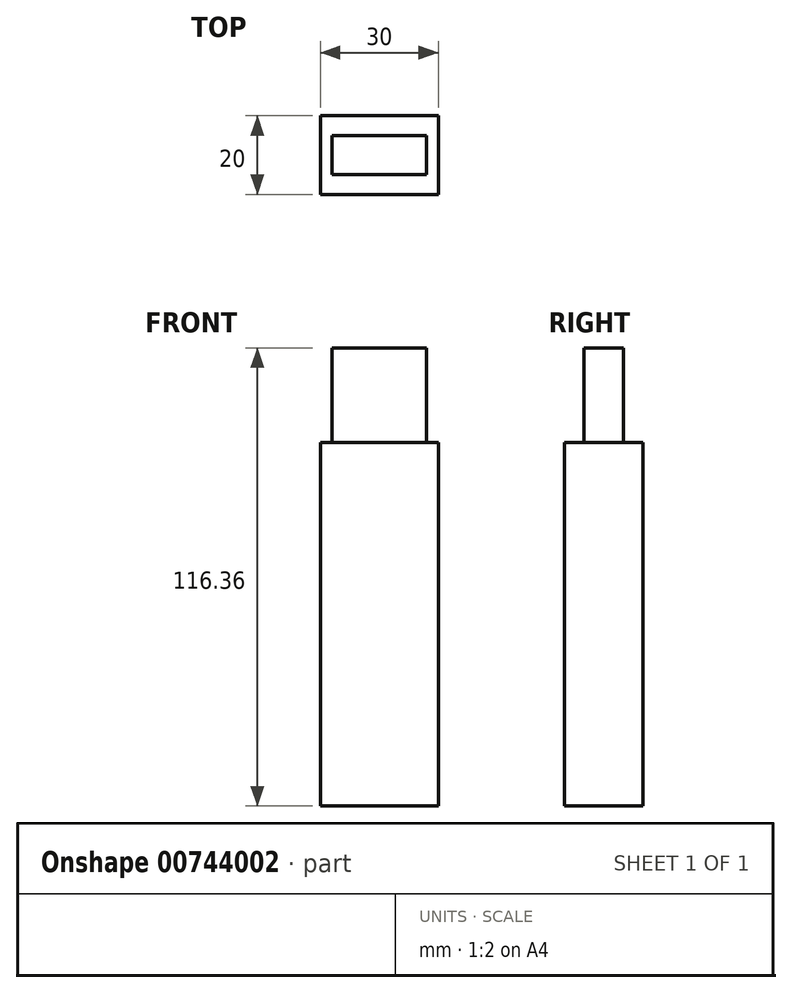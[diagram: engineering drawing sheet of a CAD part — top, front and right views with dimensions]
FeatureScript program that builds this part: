
annotation { "Feature Type Name" : "Feature", "Feature Type Description" : "" }
export const myFeature = defineFeature(function(context is Context, id is Id, definition is map)
    precondition{}
    {
        {
            var Q0;
            Q0=qCreatedBy(makeId("Front.planeOp"),FACE);
            var sketch = newSketch(context, id + "F0", { "sketchPlane" : qUnion([Q0])});
            skLineSegment(sketch, "E0.bottom", {"start": v(12, 46.18) * mm, "end": v(-12, 46.18) * mm});
            skLineSegment(sketch, "E0.top", {"start": v(12, 70.18) * mm, "end": v(-12, 70.18) * mm});
            skLineSegment(sketch, "E0.left", {"start": v(12, 46.18) * mm, "end": v(12, 70.18) * mm});
            skLineSegment(sketch, "E0.right", {"start": v(-12, 46.18) * mm, "end": v(-12, 70.18) * mm});
            skPoint(sketch, "E0.middle", {"position": v(0, 58.18) * mm});
            skLineSegment(sketch, "E1.bottom", {"start": v(-15, 46.18) * mm, "end": v(15, 46.18) * mm});
            skLineSegment(sketch, "E1.top", {"start": v(-15, -46.18) * mm, "end": v(15, -46.18) * mm});
            skLineSegment(sketch, "E1.left", {"start": v(-15, 46.18) * mm, "end": v(-15, -46.18) * mm});
            skLineSegment(sketch, "E1.right", {"start": v(15, 46.18) * mm, "end": v(15, -46.18) * mm});
            skPoint(sketch, "E1.middle", {"position": v(0, 0) * mm});
            skLineSegment(sketch, "E2.bottom", {"start": v(-15, -46.18) * mm, "end": v(0, -46.18) * mm});
            skLineSegment(sketch, "E2.top", {"start": v(-15, -78.18) * mm, "end": v(0, -78.18) * mm});
            skLineSegment(sketch, "E2.left", {"start": v(-15, -46.18) * mm, "end": v(-15, -78.18) * mm});
            skLineSegment(sketch, "E2.right", {"start": v(0, -46.18) * mm, "end": v(0, -78.18) * mm});
            skLineSegment(sketch, "E3.bottom", {"start": v(15, -46.18) * mm, "end": v(0, -46.18) * mm});
            skLineSegment(sketch, "E3.top", {"start": v(15, -78.18) * mm, "end": v(0, -78.18) * mm});
            skLineSegment(sketch, "E3.left", {"start": v(15, -46.18) * mm, "end": v(15, -78.18) * mm});
            skLineSegment(sketch, "E4.bottom", {"start": v(-15, 46.18) * mm, "end": v(-26, 46.18) * mm});
            skLineSegment(sketch, "E4.top", {"start": v(-15, -20.82) * mm, "end": v(-26, -20.82) * mm});
            skLineSegment(sketch, "E4.left", {"start": v(-15, 46.18) * mm, "end": v(-15, -20.82) * mm});
            skLineSegment(sketch, "E4.right", {"start": v(-26, 46.18) * mm, "end": v(-26, -20.82) * mm});
            skLineSegment(sketch, "E5.bottom", {"start": v(15, 46.18) * mm, "end": v(26, 46.18) * mm});
            skLineSegment(sketch, "E5.top", {"start": v(15, -20.82) * mm, "end": v(26, -20.82) * mm});
            skLineSegment(sketch, "E5.left", {"start": v(15, 46.18) * mm, "end": v(15, -20.82) * mm});
            skLineSegment(sketch, "E5.right", {"start": v(26, 46.18) * mm, "end": v(26, -20.82) * mm});
            skLineSegment(sketch, "E6.top", {"start": v(-15, -142.18) * mm, "end": v(0, -142.18) * mm});
            skLineSegment(sketch, "E6.left", {"start": v(-15, -78.18) * mm, "end": v(-15, -142.18) * mm});
            skLineSegment(sketch, "E6.right", {"start": v(0, -78.18) * mm, "end": v(0, -142.18) * mm});
            skLineSegment(sketch, "E7.top", {"start": v(15, -142.18) * mm, "end": v(0, -142.18) * mm});
            skLineSegment(sketch, "E7.left", {"start": v(15, -78.18) * mm, "end": v(15, -142.18) * mm});
            skLineSegment(sketch, "E8.bottom", {"start": v(0, -78.18) * mm, "end": v(-15, -78.18) * mm});
            skLineSegment(sketch, "E8.top", {"start": v(0, -110.18) * mm, "end": v(-15, -110.18) * mm});
            skLineSegment(sketch, "E8.left", {"start": v(0, -78.18) * mm, "end": v(0, -110.18) * mm});
            skLineSegment(sketch, "E8.right", {"start": v(-15, -78.18) * mm, "end": v(-15, -110.18) * mm});
            skLineSegment(sketch, "E9.top", {"start": v(15, -110.18) * mm, "end": v(0, -110.18) * mm});
            skLineSegment(sketch, "E9.left", {"start": v(15, -78.18) * mm, "end": v(15, -110.18) * mm});
            skSolve(sketch);
        }
        {
            var Q0;
            Q0=makeQuery(id+"F0.imprint","IMPRINT",FACE,{"disambiguationData":[TD([[makeQuery(id+"F0.imprint","IMPRINT",EDGE,{"derivedFrom":sQuery(id+"F0.wireOp",EDGE,"E1.left")}),1.0]])]});
            extrude(context, id + "F1", {"entities" : qUnion([Q0]), "depth" : 10 * mm, "offsetDistance" : 25 * mm});
        }
        {
            var Q0;
            Q0=makeQuery(id+"F0.imprint","IMPRINT",FACE,{"disambiguationData":[TD([[makeQuery(id+"F0.imprint","IMPRINT",EDGE,{"derivedFrom":sQuery(id+"F0.wireOp",EDGE,"E1.left")}),1.0]])]});
            extrude(context, id + "F2", {"entities" : qUnion([Q0]), "operationType" : NewBodyOperationType.ADD, "oppositeDirection" : true, "depth" : 10 * mm, "offsetDistance" : 25 * mm});
        }
        {
            var Q0;
            Q0=makeQuery(id+"F0.imprint","IMPRINT",FACE,{"disambiguationData":[TD([[makeQuery(id+"F0.imprint","IMPRINT",EDGE,{"derivedFrom":sQuery(id+"F0.wireOp",EDGE,"E0.top")}),1.0]])]});
            extrude(context, id + "F3", {"entities" : qUnion([Q0]), "operationType" : NewBodyOperationType.ADD, "oppositeDirection" : true, "depth" : 5 * mm, "offsetDistance" : 25 * mm});
        }
        {
            var Q0;
            Q0=makeQuery(id+"F0.imprint","IMPRINT",FACE,{"disambiguationData":[TD([[makeQuery(id+"F0.imprint","IMPRINT",EDGE,{"derivedFrom":sQuery(id+"F0.wireOp",EDGE,"E0.top")}),1.0]])]});
            extrude(context, id + "F4", {"entities" : qUnion([Q0]), "operationType" : NewBodyOperationType.ADD, "depth" : 5 * mm, "offsetDistance" : 25 * mm});
        }
    });
